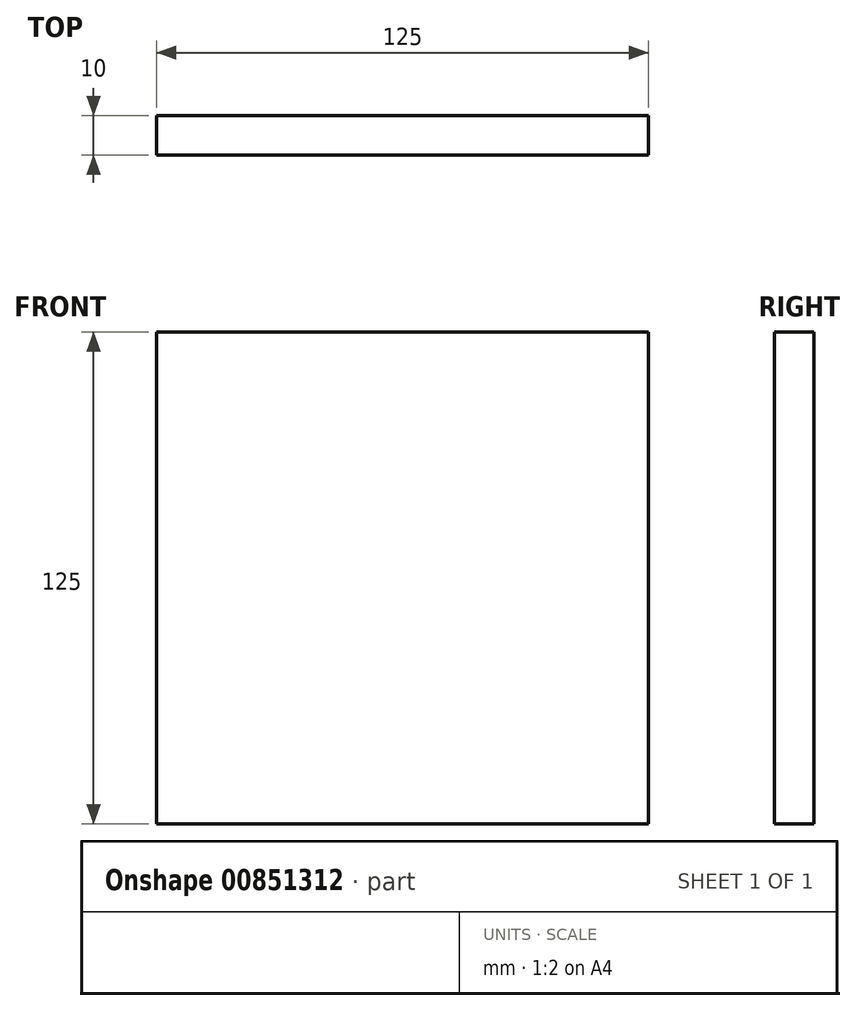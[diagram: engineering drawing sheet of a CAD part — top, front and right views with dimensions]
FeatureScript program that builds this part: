
annotation { "Feature Type Name" : "Feature", "Feature Type Description" : "" }
export const myFeature = defineFeature(function(context is Context, id is Id, definition is map)
    precondition{}
    {
        {
            var Q0;
            Q0=qCreatedBy(makeId("Front.planeOp"),FACE);
            var sketch = newSketch(context, id + "F0", { "sketchPlane" : qUnion([Q0])});
            skLineSegment(sketch, "E0.bottom", {"start": v(-125, 125) * mm, "end": v(0, 125) * mm});
            skLineSegment(sketch, "E0.top", {"start": v(-125, 0) * mm, "end": v(0, 0) * mm});
            skLineSegment(sketch, "E0.left", {"start": v(-125, 125) * mm, "end": v(-125, 0) * mm});
            skLineSegment(sketch, "E0.right", {"start": v(0, 125) * mm, "end": v(0, 0) * mm});
            skSolve(sketch);
        }
        {
            var Q0;
            Q0=makeQuery(id+"F0.imprint","IMPRINT",FACE,{"disambiguationData":[TD([[makeQuery(id+"F0.imprint","IMPRINT",EDGE,{"derivedFrom":sQuery(id+"F0.wireOp",EDGE,"E0.bottom")}),-1.0]])]});
            extrude(context, id + "F1", {"entities" : qUnion([Q0]), "depth" : 10 * mm, "offsetDistance" : 25 * mm});
        }
    });
